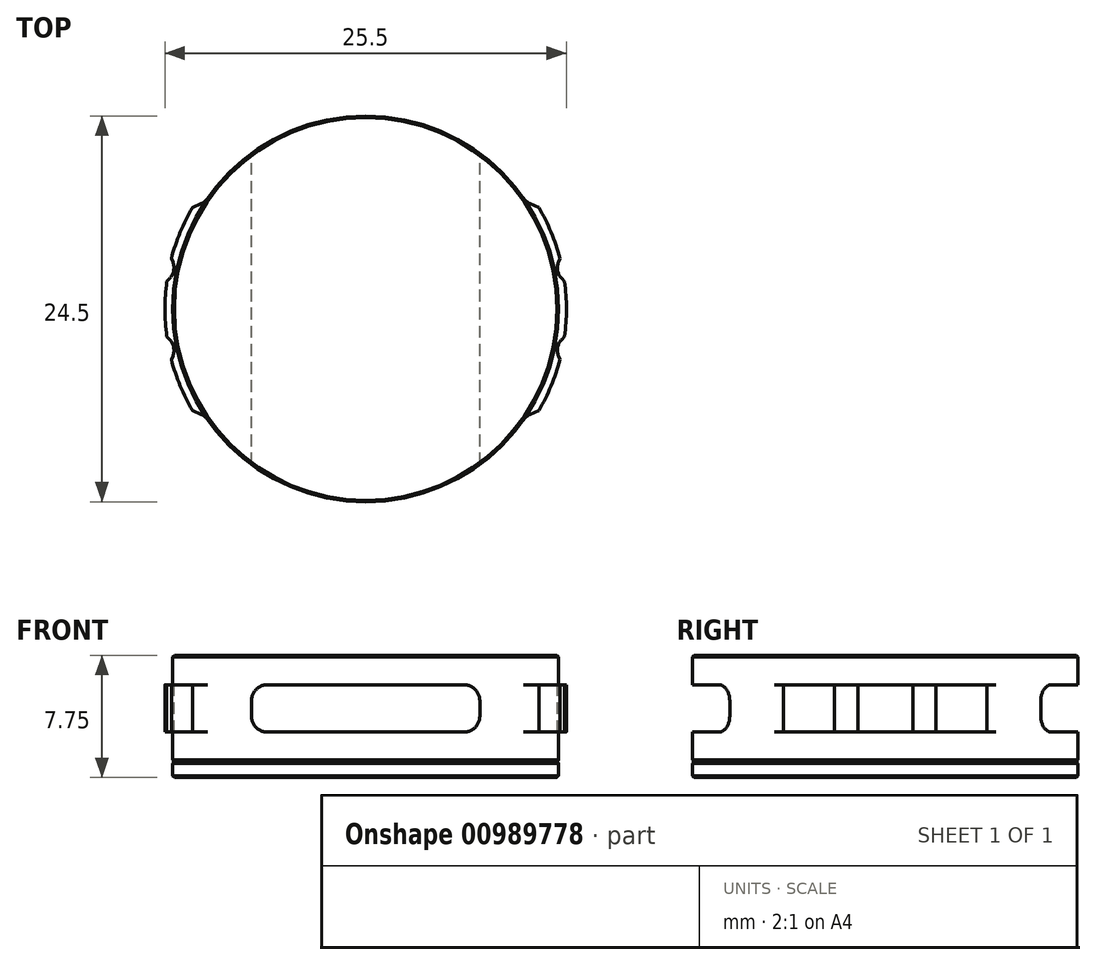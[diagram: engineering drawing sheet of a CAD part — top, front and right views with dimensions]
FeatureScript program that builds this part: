
annotation { "Feature Type Name" : "Feature", "Feature Type Description" : "" }
export const myFeature = defineFeature(function(context is Context, id is Id, definition is map)
    precondition{}
    {
        {
            var Q0;
            Q0=qCreatedBy(makeId("Top.planeOp"),FACE);
            var sketch = newSketch(context, id + "F0", { "sketchPlane" : qUnion([Q0])});
            skCircle(sketch, "E0", {"center": v(0, 0) * mm, "radius": 12.25 * mm});
            skCircle(sketch, "E1", {"center": v(0, 0) * mm, "radius": 12.75 * mm});
            skLineSegment(sketch, "E2", {"start": v(0, 0) * mm, "end": v(-12.75, 0) * mm, "construction": true});
            skLineSegment(sketch, "E3", {"start": v(-12.75, 0) * mm, "end": v(-12.63, 1.75) * mm, "construction": true});
            skLineSegment(sketch, "E4", {"start": v(-12.63, 1.75) * mm, "end": v(-12.34, 3.22) * mm, "construction": true});
            skLineSegment(sketch, "E5", {"start": v(-12.34, 3.22) * mm, "end": v(-11, 6.45) * mm, "construction": true});
            skLineSegment(sketch, "E6", {"start": v(-12.63, 1.75) * mm, "end": v(0, 0) * mm, "construction": true});
            skLineSegment(sketch, "E7", {"start": v(-12.34, 3.22) * mm, "end": v(0, 0) * mm, "construction": true});
            skLineSegment(sketch, "E8", {"start": v(-11, 6.45) * mm, "end": v(0, 0) * mm, "construction": true});
            skLineSegment(sketch, "E9", {"start": v(-12.34, 3.22) * mm, "end": v(-12.01, 2.39) * mm});
            skLineSegment(sketch, "E10", {"start": v(-12.01, 2.39) * mm, "end": v(-12.63, 1.75) * mm});
            skLineSegment(sketch, "E11", {"start": v(-12.48, 2.48) * mm, "end": v(-12.01, 2.39) * mm, "construction": true});
            skLineSegment(sketch, "E12", {"start": v(-11.67, 4.83) * mm, "end": v(-11.32, 4.69) * mm, "construction": true});
            skLineSegment(sketch, "E13.MirrorCS", {"start": v(-11, 6.45) * mm, "end": v(-10.18, 6.8) * mm});
            skLineSegment(sketch, "E14.MirrorCS", {"start": v(-12.75, 0) * mm, "end": v(-12.63, -1.75) * mm, "construction": true});
            skLineSegment(sketch, "E15.MirrorCS", {"start": v(-12.63, -1.75) * mm, "end": v(0, 0) * mm, "construction": true});
            skLineSegment(sketch, "E16.MirrorCS", {"start": v(-12.01, -2.39) * mm, "end": v(-12.63, -1.75) * mm});
            skLineSegment(sketch, "E17.MirrorCS", {"start": v(-12.63, -1.75) * mm, "end": v(-12.34, -3.22) * mm, "construction": true});
            skLineSegment(sketch, "E18.MirrorCS", {"start": v(-12.48, -2.48) * mm, "end": v(-12.01, -2.39) * mm, "construction": true});
            skLineSegment(sketch, "E19.MirrorCS", {"start": v(-12.34, -3.22) * mm, "end": v(-12.01, -2.39) * mm});
            skLineSegment(sketch, "E20.MirrorCS", {"start": v(-12.34, -3.22) * mm, "end": v(0, 0) * mm, "construction": true});
            skLineSegment(sketch, "E21.MirrorCS", {"start": v(-12.34, -3.22) * mm, "end": v(-11, -6.45) * mm, "construction": true});
            skLineSegment(sketch, "E22.MirrorCS", {"start": v(-11.67, -4.83) * mm, "end": v(-11.32, -4.69) * mm, "construction": true});
            skLineSegment(sketch, "E23.MirrorCS", {"start": v(-11, -6.45) * mm, "end": v(0, 0) * mm, "construction": true});
            skLineSegment(sketch, "E24.MirrorCS", {"start": v(-11, -6.45) * mm, "end": v(-10.18, -6.8) * mm});
            skLineSegment(sketch, "E25", {"start": v(0, 0) * mm, "end": v(0, 12.75) * mm, "construction": true});
            skLineSegment(sketch, "E26.MirrorCS", {"start": v(11, 6.45) * mm, "end": v(0, 0) * mm, "construction": true});
            skLineSegment(sketch, "E27.MirrorCS", {"start": v(12.34, 3.22) * mm, "end": v(0, 0) * mm, "construction": true});
            skLineSegment(sketch, "E28.MirrorCS", {"start": v(12.63, 1.75) * mm, "end": v(0, 0) * mm, "construction": true});
            skLineSegment(sketch, "E29.MirrorCS", {"start": v(0, 0) * mm, "end": v(12.75, 0) * mm, "construction": true});
            skLineSegment(sketch, "E30.MirrorCS", {"start": v(12.63, -1.75) * mm, "end": v(0, 0) * mm, "construction": true});
            skLineSegment(sketch, "E31.MirrorCS", {"start": v(12.34, -3.22) * mm, "end": v(0, 0) * mm, "construction": true});
            skLineSegment(sketch, "E32.MirrorCS", {"start": v(11, -6.45) * mm, "end": v(0, 0) * mm, "construction": true});
            skLineSegment(sketch, "E33.MirrorCS", {"start": v(11, -6.45) * mm, "end": v(10.18, -6.8) * mm});
            skLineSegment(sketch, "E34.MirrorCS", {"start": v(12.34, -3.22) * mm, "end": v(11, -6.45) * mm, "construction": true});
            skLineSegment(sketch, "E35.MirrorCS", {"start": v(11.67, -4.83) * mm, "end": v(11.32, -4.69) * mm, "construction": true});
            skLineSegment(sketch, "E36.MirrorCS", {"start": v(12.34, -3.22) * mm, "end": v(12.01, -2.39) * mm});
            skLineSegment(sketch, "E37.MirrorCS", {"start": v(12.48, -2.48) * mm, "end": v(12.01, -2.39) * mm, "construction": true});
            skLineSegment(sketch, "E38.MirrorCS", {"start": v(12.01, -2.39) * mm, "end": v(12.63, -1.75) * mm});
            skLineSegment(sketch, "E39.MirrorCS", {"start": v(12.63, -1.75) * mm, "end": v(12.34, -3.22) * mm, "construction": true});
            skLineSegment(sketch, "E40.MirrorCS", {"start": v(12.75, 0) * mm, "end": v(12.63, -1.75) * mm, "construction": true});
            skLineSegment(sketch, "E41.MirrorCS", {"start": v(12.75, 0) * mm, "end": v(12.63, 1.75) * mm, "construction": true});
            skLineSegment(sketch, "E42.MirrorCS", {"start": v(12.01, 2.39) * mm, "end": v(12.63, 1.75) * mm});
            skLineSegment(sketch, "E43.MirrorCS", {"start": v(12.48, 2.48) * mm, "end": v(12.01, 2.39) * mm, "construction": true});
            skLineSegment(sketch, "E44.MirrorCS", {"start": v(12.34, 3.22) * mm, "end": v(12.01, 2.39) * mm});
            skLineSegment(sketch, "E45.MirrorCS", {"start": v(12.34, 3.22) * mm, "end": v(11, 6.45) * mm, "construction": true});
            skLineSegment(sketch, "E46.MirrorCS", {"start": v(11.67, 4.83) * mm, "end": v(11.32, 4.69) * mm, "construction": true});
            skLineSegment(sketch, "E47.MirrorCS", {"start": v(11, 6.45) * mm, "end": v(10.18, 6.8) * mm});
            skSolve(sketch);
        }
        {
            var Q0;
            Q0=qCreatedBy(makeId("Top.planeOp"),FACE);
            cPlane(context, id + "F1", {"entities" : qUnion([Q0]), "cplaneType" : CPlaneType.OFFSET, "offset" : (3.75 / 2) * mm, "width" : 150 * mm, "height" : 150 * mm});
        }
        {
            var Q0;
            Q0=qCreatedBy(id+"F1.planeOp",FACE);
            var sketch = newSketch(context, id + "F2", { "sketchPlane" : qUnion([Q0])});
            skCircle(sketch, "E48", {"center": v(0, 0) * mm, "radius": 12.25 * mm});
            skCircle(sketch, "E49", {"center": v(0, 0) * mm, "radius": 12.75 * mm});
            skLineSegment(sketch, "E50", {"start": v(0, 0) * mm, "end": v(-12.75, 0) * mm, "construction": true});
            skLineSegment(sketch, "E51", {"start": v(-12.75, 0) * mm, "end": v(-12.63, 1.75) * mm, "construction": true});
            skLineSegment(sketch, "E52", {"start": v(-12.63, 1.75) * mm, "end": v(-12.34, 3.22) * mm, "construction": true});
            skLineSegment(sketch, "E53", {"start": v(-12.34, 3.22) * mm, "end": v(-11, 6.45) * mm, "construction": true});
            skLineSegment(sketch, "E54", {"start": v(-12.63, 1.75) * mm, "end": v(0, 0) * mm, "construction": true});
            skLineSegment(sketch, "E55", {"start": v(-12.34, 3.22) * mm, "end": v(0, 0) * mm, "construction": true});
            skLineSegment(sketch, "E56", {"start": v(-11, 6.45) * mm, "end": v(0, 0) * mm, "construction": true});
            skLineSegment(sketch, "E57", {"start": v(-12.34, 3.22) * mm, "end": v(-12.01, 2.39) * mm});
            skLineSegment(sketch, "E58", {"start": v(-12.01, 2.39) * mm, "end": v(-12.63, 1.75) * mm});
            skLineSegment(sketch, "E59", {"start": v(-12.48, 2.48) * mm, "end": v(-12.01, 2.39) * mm, "construction": true});
            skLineSegment(sketch, "E60", {"start": v(-11.67, 4.83) * mm, "end": v(-11.32, 4.69) * mm, "construction": true});
            skLineSegment(sketch, "E61.MirrorCS", {"start": v(-11, 6.45) * mm, "end": v(-10.18, 6.8) * mm});
            skLineSegment(sketch, "E62.MirrorCS", {"start": v(-12.75, 0) * mm, "end": v(-12.63, -1.75) * mm, "construction": true});
            skLineSegment(sketch, "E63.MirrorCS", {"start": v(-12.63, -1.75) * mm, "end": v(0, 0) * mm, "construction": true});
            skLineSegment(sketch, "E64.MirrorCS", {"start": v(-12.01, -2.39) * mm, "end": v(-12.63, -1.75) * mm});
            skLineSegment(sketch, "E65.MirrorCS", {"start": v(-12.63, -1.75) * mm, "end": v(-12.34, -3.22) * mm, "construction": true});
            skLineSegment(sketch, "E66.MirrorCS", {"start": v(-12.48, -2.48) * mm, "end": v(-12.01, -2.39) * mm, "construction": true});
            skLineSegment(sketch, "E67.MirrorCS", {"start": v(-12.34, -3.22) * mm, "end": v(-12.01, -2.39) * mm});
            skLineSegment(sketch, "E68.MirrorCS", {"start": v(-12.34, -3.22) * mm, "end": v(0, 0) * mm, "construction": true});
            skLineSegment(sketch, "E69.MirrorCS", {"start": v(-12.34, -3.22) * mm, "end": v(-11, -6.45) * mm, "construction": true});
            skLineSegment(sketch, "E70.MirrorCS", {"start": v(-11.67, -4.83) * mm, "end": v(-11.32, -4.69) * mm, "construction": true});
            skLineSegment(sketch, "E71.MirrorCS", {"start": v(-11, -6.45) * mm, "end": v(0, 0) * mm, "construction": true});
            skLineSegment(sketch, "E72.MirrorCS", {"start": v(-11, -6.45) * mm, "end": v(-10.18, -6.8) * mm});
            skLineSegment(sketch, "E73", {"start": v(0, 0) * mm, "end": v(0, 12.75) * mm, "construction": true});
            skLineSegment(sketch, "E74.MirrorCS", {"start": v(11, 6.45) * mm, "end": v(0, 0) * mm, "construction": true});
            skLineSegment(sketch, "E75.MirrorCS", {"start": v(12.34, 3.22) * mm, "end": v(0, 0) * mm, "construction": true});
            skLineSegment(sketch, "E76.MirrorCS", {"start": v(12.63, 1.75) * mm, "end": v(0, 0) * mm, "construction": true});
            skLineSegment(sketch, "E77.MirrorCS", {"start": v(0, 0) * mm, "end": v(12.75, 0) * mm, "construction": true});
            skLineSegment(sketch, "E78.MirrorCS", {"start": v(12.63, -1.75) * mm, "end": v(0, 0) * mm, "construction": true});
            skLineSegment(sketch, "E79.MirrorCS", {"start": v(12.34, -3.22) * mm, "end": v(0, 0) * mm, "construction": true});
            skLineSegment(sketch, "E80.MirrorCS", {"start": v(11, -6.45) * mm, "end": v(0, 0) * mm, "construction": true});
            skLineSegment(sketch, "E81.MirrorCS", {"start": v(11, -6.45) * mm, "end": v(10.18, -6.8) * mm});
            skLineSegment(sketch, "E82.MirrorCS", {"start": v(12.34, -3.22) * mm, "end": v(11, -6.45) * mm, "construction": true});
            skLineSegment(sketch, "E83.MirrorCS", {"start": v(11.67, -4.83) * mm, "end": v(11.32, -4.69) * mm, "construction": true});
            skLineSegment(sketch, "E84.MirrorCS", {"start": v(12.34, -3.22) * mm, "end": v(12.01, -2.39) * mm});
            skLineSegment(sketch, "E85.MirrorCS", {"start": v(12.48, -2.48) * mm, "end": v(12.01, -2.39) * mm, "construction": true});
            skLineSegment(sketch, "E86.MirrorCS", {"start": v(12.01, -2.39) * mm, "end": v(12.63, -1.75) * mm});
            skLineSegment(sketch, "E87.MirrorCS", {"start": v(12.63, -1.75) * mm, "end": v(12.34, -3.22) * mm, "construction": true});
            skLineSegment(sketch, "E88.MirrorCS", {"start": v(12.75, 0) * mm, "end": v(12.63, -1.75) * mm, "construction": true});
            skLineSegment(sketch, "E89.MirrorCS", {"start": v(12.75, 0) * mm, "end": v(12.63, 1.75) * mm, "construction": true});
            skLineSegment(sketch, "E90.MirrorCS", {"start": v(12.01, 2.39) * mm, "end": v(12.63, 1.75) * mm});
            skLineSegment(sketch, "E91.MirrorCS", {"start": v(12.48, 2.48) * mm, "end": v(12.01, 2.39) * mm, "construction": true});
            skLineSegment(sketch, "E92.MirrorCS", {"start": v(12.34, 3.22) * mm, "end": v(12.01, 2.39) * mm});
            skLineSegment(sketch, "E93.MirrorCS", {"start": v(12.34, 3.22) * mm, "end": v(11, 6.45) * mm, "construction": true});
            skLineSegment(sketch, "E94.MirrorCS", {"start": v(11.67, 4.83) * mm, "end": v(11.32, 4.69) * mm, "construction": true});
            skLineSegment(sketch, "E95.MirrorCS", {"start": v(11, 6.45) * mm, "end": v(10.18, 6.8) * mm});
            skSolve(sketch);
        }
        {
            var Q0;
            {var subQ0=sQuery(id+"F2.wireOp",EDGE,"E48");var subQ3=makeQuery(id+"F2.imprint","INTERSECT",VERTEX,{"derivedFrom":[subQ0,sQuery(id+"F2.wireOp",EDGE,"E61.MirrorCS")]});Q0=makeQuery(id+"F2.imprint","IMPRINT",FACE,{"disambiguationData":[TD([[makeQuery(id+"F2.imprint","IMPRINT",EDGE,{"disambiguationData":[TD([[subQ3,1.0]])],"derivedFrom":subQ0}),1.0]])]});}
            var Q1;
            {var subQ0=sQuery(id+"F2.wireOp",EDGE,"E57");Q1=makeQuery(id+"F2.imprint","IMPRINT",FACE,{"disambiguationData":[TD([[makeQuery(id+"F2.imprint","IMPRINT",EDGE,{"derivedFrom":subQ0}),1.0]])]});}
            var Q2;
            {var subQ0=sQuery(id+"F2.wireOp",EDGE,"E58");Q2=makeQuery(id+"F2.imprint","IMPRINT",FACE,{"disambiguationData":[TD([[makeQuery(id+"F2.imprint","IMPRINT",EDGE,{"derivedFrom":subQ0}),1.0]])]});}
            var Q3;
            {var subQ0=sQuery(id+"F2.wireOp",EDGE,"E67.MirrorCS");Q3=makeQuery(id+"F2.imprint","IMPRINT",FACE,{"disambiguationData":[TD([[makeQuery(id+"F2.imprint","IMPRINT",EDGE,{"derivedFrom":subQ0}),-1.0]])]});}
            var Q4;
            {var subQ0=sQuery(id+"F2.wireOp",EDGE,"E81.MirrorCS");Q4=makeQuery(id+"F2.imprint","IMPRINT",FACE,{"disambiguationData":[TD([[makeQuery(id+"F2.imprint","IMPRINT",EDGE,{"derivedFrom":subQ0}),-1.0]])]});}
            var Q5;
            {var subQ0=sQuery(id+"F2.wireOp",EDGE,"E86.MirrorCS");Q5=makeQuery(id+"F2.imprint","IMPRINT",FACE,{"disambiguationData":[TD([[makeQuery(id+"F2.imprint","IMPRINT",EDGE,{"derivedFrom":subQ0}),1.0]])]});}
            var Q6;
            {var subQ0=sQuery(id+"F2.wireOp",EDGE,"E92.MirrorCS");Q6=makeQuery(id+"F2.imprint","IMPRINT",FACE,{"disambiguationData":[TD([[makeQuery(id+"F2.imprint","IMPRINT",EDGE,{"derivedFrom":subQ0}),-1.0]])]});}
            extrude(context, id + "F3", {"entities" : qUnion([Q0, Q1, Q2, Q3, Q4, Q5, Q6]), "depth" : 3 * mm, "offsetDistance" : 25 * mm});
        }
        {
            var Q0;
            {var subQ0=sQuery(id+"F0.wireOp",EDGE,"E0");var subQ3=makeQuery(id+"F0.imprint","INTERSECT",VERTEX,{"derivedFrom":[subQ0,sQuery(id+"F0.wireOp",EDGE,"E13.MirrorCS")]});Q0=makeQuery(id+"F0.imprint","IMPRINT",FACE,{"disambiguationData":[TD([[makeQuery(id+"F0.imprint","IMPRINT",EDGE,{"disambiguationData":[TD([[subQ3,1.0]])],"derivedFrom":subQ0}),1.0]])]});}
            extrude(context, id + "F4", {"entities" : qUnion([Q0]), "operationType" : NewBodyOperationType.ADD, "depth" : 6.75 * mm, "offsetDistance" : 25 * mm});
        }
        {
            var Q0;
            Q0=qCreatedBy(makeId("Front.planeOp"),FACE);
            var sketch = newSketch(context, id + "F5", { "sketchPlane" : qUnion([Q0])});
            skLineSegment(sketch, "E96", {"start": v(0, 0) * mm, "end": v(0, 6.75) * mm, "construction": true});
            skLineSegment(sketch, "E97.bottom", {"start": v(-7.25, 1.87) * mm, "end": v(7.25, 1.87) * mm});
            skLineSegment(sketch, "E97.top", {"start": v(-7.25, 4.87) * mm, "end": v(7.25, 4.87) * mm});
            skLineSegment(sketch, "E97.left", {"start": v(-7.25, 1.87) * mm, "end": v(-7.25, 4.87) * mm});
            skLineSegment(sketch, "E97.right", {"start": v(7.25, 1.87) * mm, "end": v(7.25, 4.87) * mm});
            skPoint(sketch, "E97.middle", {"position": v(0, 3.38) * mm});
            skSolve(sketch);
        }
        {
            var Q0;
            Q0=makeQuery(id+"F5.imprint","IMPRINT",FACE,{"disambiguationData":[TD([[makeQuery(id+"F5.imprint","IMPRINT",EDGE,{"derivedFrom":sQuery(id+"F5.wireOp",EDGE,"E97.bottom")}),1.0]])]});
            extrude(context, id + "F6", {"entities" : qUnion([Q0]), "operationType" : NewBodyOperationType.REMOVE, "endBound" : BoundingType.SYMMETRIC, "depth" : 50 * mm, "offsetDistance" : 25 * mm});
        }
        {
            var Q0;
            Q0=makeQuery(id+"F6.boolean.opBoolean","COPY",EDGE,{"derivedFrom":makeQuery(id+"F6.opExtrude","SWEPT_EDGE",EDGE,{"disambiguationData":[OSD([sQuery(id+"F5.wireOp",EDGE,"E97.bottom"),sQuery(id+"F5.wireOp",EDGE,"E97.left")])]})});
            var Q1;
            Q1=makeQuery(id+"F6.boolean.opBoolean","COPY",EDGE,{"derivedFrom":makeQuery(id+"F6.opExtrude","SWEPT_EDGE",EDGE,{"disambiguationData":[OSD([sQuery(id+"F5.wireOp",EDGE,"E97.top"),sQuery(id+"F5.wireOp",EDGE,"E97.left")])]})});
            var Q2;
            Q2=makeQuery(id+"F6.boolean.opBoolean","COPY",EDGE,{"derivedFrom":makeQuery(id+"F6.opExtrude","SWEPT_EDGE",EDGE,{"disambiguationData":[OSD([sQuery(id+"F5.wireOp",EDGE,"E97.top"),sQuery(id+"F5.wireOp",EDGE,"E97.right")])]})});
            var Q3;
            Q3=makeQuery(id+"F6.boolean.opBoolean","COPY",EDGE,{"derivedFrom":makeQuery(id+"F6.opExtrude","SWEPT_EDGE",EDGE,{"disambiguationData":[OSD([sQuery(id+"F5.wireOp",EDGE,"E97.bottom"),sQuery(id+"F5.wireOp",EDGE,"E97.right")])]})});
            fillet(context, id + "F7", {"entities" : qUnion([Q0, Q1, Q2, Q3]), "radius" : 1 * mm, "tangentPropagation" : true, "allowEdgeOverflow" : false});
        }
        {
            var Q0;
            {var subQ0=sQuery(id+"F0.wireOp",EDGE,"E0");var subQ3=makeQuery(id+"F0.imprint","INTERSECT",VERTEX,{"derivedFrom":[subQ0,sQuery(id+"F0.wireOp",EDGE,"E13.MirrorCS")]});Q0=makeQuery(id+"F0.imprint","IMPRINT",FACE,{"disambiguationData":[TD([[makeQuery(id+"F0.imprint","IMPRINT",EDGE,{"disambiguationData":[TD([[subQ3,1.0]])],"derivedFrom":subQ0}),1.0]])]});}
            extrude(context, id + "F8", {"entities" : qUnion([Q0]), "oppositeDirection" : true, "depth" : 1 * mm, "offsetDistance" : 25 * mm});
        }
        {
            var Q0;
            Q0=makeQuery(id+"F8.opExtrude","CAP_EDGE",EDGE,{"disambiguationData":[OSD([sQuery(id+"F0.wireOp",EDGE,"E0")])],"isStart":false});
            var Q1;
            Q1=makeQuery(id+"F4.opExtrude","CAP_EDGE",EDGE,{"disambiguationData":[OSD([sQuery(id+"F0.wireOp",EDGE,"E0")])],"isStart":true});
            var Q2;
            Q2=makeQuery(id+"F8.opExtrude","SWEPT_FACE",FACE,{"disambiguationData":[OSD([sQuery(id+"F0.wireOp",EDGE,"E0")])]});
            var Q3;
            Q3=makeQuery(id+"F4.opExtrude","CAP_EDGE",EDGE,{"disambiguationData":[OSD([sQuery(id+"F0.wireOp",EDGE,"E0")])],"isStart":false});
            chamfer(context, id + "F9", {"entities" : qUnion([Q0, Q1, Q2, Q3]), "width" : .1 * mm, "tangentPropagation" : true});
        }
        {
            var Q0;
            Q0=makeQuery(id+"F3.opExtrude","SWEPT_EDGE",EDGE,{"disambiguationData":[OSD([sQuery(id+"F2.wireOp",EDGE,"E48"),sQuery(id+"F2.wireOp",EDGE,"E84.MirrorCS"),sQuery(id+"F2.wireOp",EDGE,"E86.MirrorCS")])]});
            var Q1;
            Q1=makeQuery(id+"F3.opExtrude","SWEPT_EDGE",EDGE,{"disambiguationData":[OSD([sQuery(id+"F2.wireOp",EDGE,"E48"),sQuery(id+"F2.wireOp",EDGE,"E90.MirrorCS"),sQuery(id+"F2.wireOp",EDGE,"E92.MirrorCS")])]});
            var Q2;
            Q2=makeQuery(id+"F3.opExtrude","SWEPT_EDGE",EDGE,{"disambiguationData":[OSD([sQuery(id+"F2.wireOp",EDGE,"E48"),sQuery(id+"F2.wireOp",EDGE,"E57"),sQuery(id+"F2.wireOp",EDGE,"E58")])]});
            var Q3;
            Q3=makeQuery(id+"F3.opExtrude","SWEPT_EDGE",EDGE,{"disambiguationData":[OSD([sQuery(id+"F2.wireOp",EDGE,"E48"),sQuery(id+"F2.wireOp",EDGE,"E64.MirrorCS"),sQuery(id+"F2.wireOp",EDGE,"E67.MirrorCS")])]});
            var Q4;
            Q4=makeQuery(id+"F3.opExtrude","SWEPT_EDGE",EDGE,{"disambiguationData":[OSD([sQuery(id+"F2.wireOp",EDGE,"E48"),sQuery(id+"F2.wireOp",EDGE,"E72.MirrorCS")])]});
            var Q5;
            Q5=makeQuery(id+"F3.opExtrude","SWEPT_EDGE",EDGE,{"disambiguationData":[OSD([sQuery(id+"F2.wireOp",EDGE,"E48"),sQuery(id+"F2.wireOp",EDGE,"E61.MirrorCS")])]});
            var Q6;
            Q6=makeQuery(id+"F3.opExtrude","SWEPT_EDGE",EDGE,{"disambiguationData":[OSD([sQuery(id+"F2.wireOp",EDGE,"E48"),sQuery(id+"F2.wireOp",EDGE,"E95.MirrorCS")])]});
            var Q7;
            Q7=makeQuery(id+"F3.opExtrude","SWEPT_EDGE",EDGE,{"disambiguationData":[OSD([sQuery(id+"F2.wireOp",EDGE,"E48"),sQuery(id+"F2.wireOp",EDGE,"E81.MirrorCS")])]});
            fillet(context, id + "F10", {"entities" : qUnion([Q0, Q1, Q2, Q3, Q4, Q5, Q6, Q7]), "radius" : 1 * mm, "tangentPropagation" : true, "allowEdgeOverflow" : false});
        }
    });
